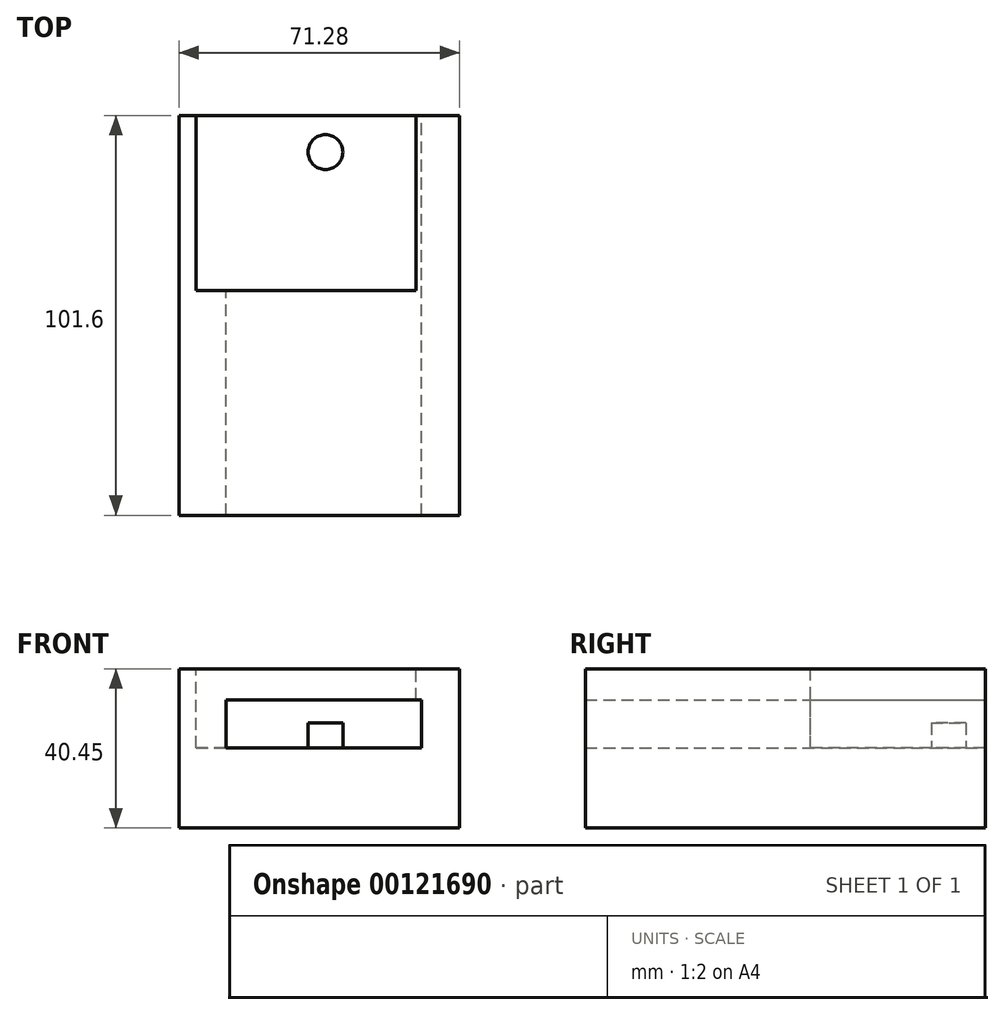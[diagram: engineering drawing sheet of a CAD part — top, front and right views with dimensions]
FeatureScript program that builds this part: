
annotation { "Feature Type Name" : "Feature", "Feature Type Description" : "" }
export const myFeature = defineFeature(function(context is Context, id is Id, definition is map)
    precondition{}
    {
        {
            var Q0;
            Q0=qCreatedBy(makeId("Front.planeOp"),FACE);
            var sketch = newSketch(context, id + "F0", { "sketchPlane" : qUnion([Q0])});
            skLineSegment(sketch, "E0.bottom", {"start": v(-37.24, 20.08) * mm, "end": v(34.04, 20.08) * mm});
            skLineSegment(sketch, "E0.top", {"start": v(-37.24, -20.37) * mm, "end": v(34.04, -20.37) * mm});
            skLineSegment(sketch, "E0.left", {"start": v(-37.24, 20.08) * mm, "end": v(-37.24, -20.37) * mm});
            skLineSegment(sketch, "E0.right", {"start": v(34.04, 20.08) * mm, "end": v(34.04, -20.37) * mm});
            skSolve(sketch);
        }
        {
            var Q0;
            Q0=qCreatedBy(makeId("Front.planeOp"),FACE);
            var sketch = newSketch(context, id + "F1", { "sketchPlane" : qUnion([Q0])});
            skLineSegment(sketch, "E1.bottom", {"start": v(-25.31, 12.22) * mm, "end": v(24.44, 12.22) * mm});
            skLineSegment(sketch, "E1.top", {"start": v(-25.31, 0) * mm, "end": v(24.44, 0) * mm});
            skLineSegment(sketch, "E1.left", {"start": v(-25.31, 12.22) * mm, "end": v(-25.31, 0) * mm});
            skLineSegment(sketch, "E1.right", {"start": v(24.44, 12.22) * mm, "end": v(24.44, 0) * mm});
            skSolve(sketch);
        }
        {
            var Q0;
            Q0=makeQuery(id+"F0.imprint","IMPRINT",FACE,{"disambiguationData":[TD([[makeQuery(id+"F0.imprint","IMPRINT",EDGE,{"derivedFrom":sQuery(id+"F0.wireOp",EDGE,"E0.bottom")}),-1.0]])]});
            extrude(context, id + "F2", {"entities" : qUnion([Q0]), "depth" : 101.6 * mm});
        }
        {
            var Q0;
            Q0=makeQuery(id+"F1.imprint","IMPRINT",FACE,{"disambiguationData":[TD([[makeQuery(id+"F1.imprint","IMPRINT",EDGE,{"derivedFrom":sQuery(id+"F1.wireOp",EDGE,"E1.bottom")}),-1.0]])]});
            extrude(context, id + "F3", {"entities" : qUnion([Q0]), "operationType" : NewBodyOperationType.REMOVE, "depth" : 101.6 * mm});
        }
        {
            var Q0;
            Q0=qCreatedBy(makeId("Top.planeOp"),FACE);
            var sketch = newSketch(context, id + "F4", { "sketchPlane" : qUnion([Q0])});
            skCircle(sketch, "E2", {"center": v(0, -9.3) * mm, "radius": 4.41 * mm});
            skSolve(sketch);
        }
        {
            var Q0;
            Q0 = qSketchRegion(id + "F4", true);
            var Q1;
            Q1=sQuery(id+"F4.wireOp",EDGE,"E2");
            extrude(context, id + "F5", {"entities" : qUnion([Q0]), "operationType" : NewBodyOperationType.ADD, "surfaceEntities" : qUnion([Q1]), "depth" : 6.35 * mm});
        }
        {
            var Q0;
            Q0=qCreatedBy(makeId("Top.planeOp"),FACE);
            var sketch = newSketch(context, id + "F6", { "sketchPlane" : qUnion([Q0])});
            skLineSegment(sketch, "E3.bottom", {"start": v(23, 0.25) * mm, "end": v(-32.86, 0.25) * mm});
            skLineSegment(sketch, "E3.top", {"start": v(23, -44.52) * mm, "end": v(-32.86, -44.52) * mm});
            skLineSegment(sketch, "E3.left", {"start": v(23, 0.25) * mm, "end": v(23, -44.52) * mm});
            skLineSegment(sketch, "E3.right", {"start": v(-32.86, 0.25) * mm, "end": v(-32.86, -44.52) * mm});
            skSolve(sketch);
        }
        {
            var Q0;
            Q0 = qSketchRegion(id + "F6", true);
            var Q1;
            Q1 = qConstructionFilter(qBodyType(qCreatedBy(id + "F6" ,EDGE), BodyType.WIRE), ConstructionObject.NO);
            extrude(context, id + "F7", {"entities" : qUnion([Q0]), "operationType" : NewBodyOperationType.REMOVE, "surfaceEntities" : qUnion([Q1]), "depth" : 101.6 * mm});
        }
        {
            var Q0;
            Q0 = qSketchRegion(id + "F4", true);
            extrude(context, id + "F8", {"entities" : qUnion([Q0]), "operationType" : NewBodyOperationType.ADD, "depth" : 6.35 * mm});
        }
    });
